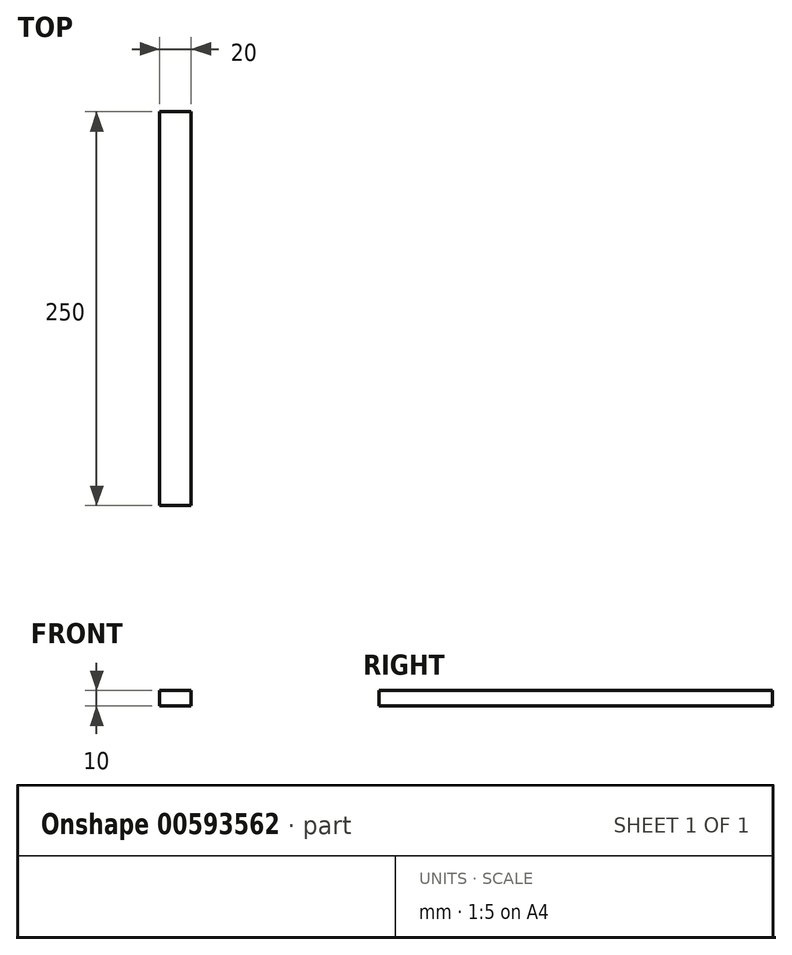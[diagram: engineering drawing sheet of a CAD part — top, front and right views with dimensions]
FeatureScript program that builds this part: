
annotation { "Feature Type Name" : "Feature", "Feature Type Description" : "" }
export const myFeature = defineFeature(function(context is Context, id is Id, definition is map)
    precondition{}
    {
        {
            var Q0;
            Q0=qCreatedBy(makeId("Top.planeOp"),FACE);
            var sketch = newSketch(context, id + "F0", { "sketchPlane" : qUnion([Q0])});
            skLineSegment(sketch, "E0.bottom", {"start": v(-35.9, -124.32) * mm, "end": v(-55.9, -124.32) * mm});
            skLineSegment(sketch, "E0.top", {"start": v(-35.9, 125.68) * mm, "end": v(-55.9, 125.68) * mm});
            skLineSegment(sketch, "E0.left", {"start": v(-35.9, -124.32) * mm, "end": v(-35.9, 125.68) * mm});
            skLineSegment(sketch, "E0.right", {"start": v(-55.9, -124.32) * mm, "end": v(-55.9, 125.68) * mm});
            skSolve(sketch);
        }
        {
            var Q0;
            Q0=makeQuery(id+"F0.imprint","IMPRINT",FACE,{"disambiguationData":[TD([[makeQuery(id+"F0.imprint","IMPRINT",EDGE,{"derivedFrom":sQuery(id+"F0.wireOp",EDGE,"E0.bottom")}),-1.0]])]});
            extrude(context, id + "F1", {"entities" : qUnion([Q0]), "depth" : 10 * mm, "offsetDistance" : 25.4 * mm});
        }
    });
